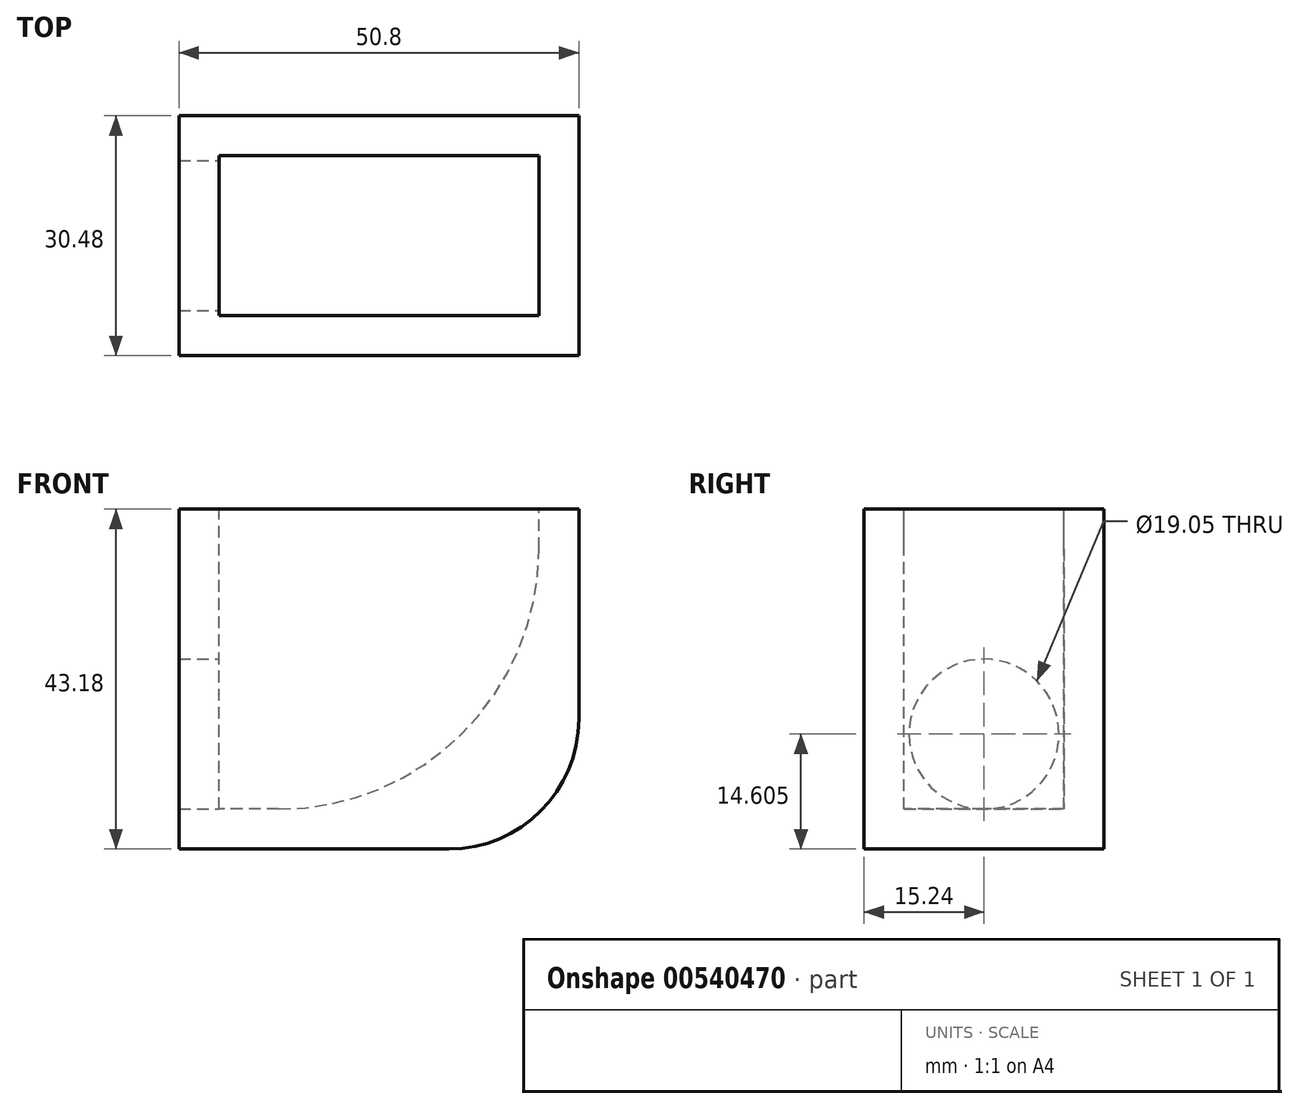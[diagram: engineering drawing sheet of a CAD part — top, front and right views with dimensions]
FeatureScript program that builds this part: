
annotation { "Feature Type Name" : "Feature", "Feature Type Description" : "" }
export const myFeature = defineFeature(function(context is Context, id is Id, definition is map)
    precondition{}
    {
        {
            var Q0;
            Q0=qCreatedBy(makeId("Front.planeOp"),FACE);
            var sketch = newSketch(context, id + "F0", { "sketchPlane" : qUnion([Q0])});
            skLineSegment(sketch, "E0", {"start": v(0, 0) * mm, "end": v(50.8, 0) * mm});
            skLineSegment(sketch, "E1", {"start": v(50.8, 0) * mm, "end": v(50.8, -43.18) * mm});
            skLineSegment(sketch, "E2", {"start": v(50.8, -43.18) * mm, "end": v(0, -43.18) * mm});
            skLineSegment(sketch, "E3", {"start": v(0, 0) * mm, "end": v(0, -43.18) * mm});
            skSolve(sketch);
        }
        {
            var Q0;
            Q0 = qSketchRegion(id + "F0", true);
            extrude(context, id + "F1", {"entities" : qUnion([Q0]), "depth" : 30.48 * mm, "offsetDistance" : 25.4 * mm});
        }
        {
            var Q0;
            Q0=makeQuery(id+"F1.opExtrude","SWEPT_EDGE",EDGE,{"disambiguationData":[OSD([sQuery(id+"F0.wireOp",EDGE,"E1"),sQuery(id+"F0.wireOp",EDGE,"E2")])]});
            fillet(context, id + "F2", {"entities" : qUnion([Q0]), "radius" : 16.5 * mm, "tangentPropagation" : true, "allowEdgeOverflow" : false});
        }
        {
            var Q0;
            Q0=makeQuery(id+"F1.opExtrude","SWEPT_FACE",FACE,{"disambiguationData":[OSD([sQuery(id+"F0.wireOp",EDGE,"E0")])]});
            var sketch = newSketch(context, id + "F3", { "sketchPlane" : qUnion([Q0])});
            skLineSegment(sketch, "E4", {"start": v(5.08, -5.08) * mm, "end": v(5.08, -25.4) * mm});
            skLineSegment(sketch, "E5", {"start": v(5.08, -25.4) * mm, "end": v(45.72, -25.4) * mm});
            skLineSegment(sketch, "E6", {"start": v(45.72, -25.4) * mm, "end": v(45.72, -5.08) * mm});
            skLineSegment(sketch, "E7", {"start": v(45.72, -5.08) * mm, "end": v(5.08, -5.08) * mm});
            skSolve(sketch);
        }
        {
            var Q0;
            Q0=makeQuery(id+"F3.imprint","IMPRINT",FACE,{"disambiguationData":[TD([[makeQuery(id+"F3.imprint","IMPRINT",EDGE,{"derivedFrom":sQuery(id+"F3.wireOp",EDGE,"E4")}),1.0]])]});
            extrude(context, id + "F4", {"entities" : qUnion([Q0]), "operationType" : NewBodyOperationType.REMOVE, "oppositeDirection" : true, "depth" : 38.1 * mm, "offsetDistance" : 25.4 * mm});
        }
        {
            var Q0;
            Q0=makeQuery(id+"F1.opExtrude","SWEPT_FACE",FACE,{"disambiguationData":[OSD([sQuery(id+"F0.wireOp",EDGE,"E3")])]});
            var sketch = newSketch(context, id + "F5", { "sketchPlane" : qUnion([Q0])});
            skCircle(sketch, "E8", {"center": v(15.24, -33.66) * mm, "radius": 9.53 * mm});
            skPoint(sketch, "E8.centerSnap0", {"position": v(15.24, -43.18) * mm});
            skSolve(sketch);
        }
        {
            var Q0;
            Q0=makeQuery(id+"F5.imprint","IMPRINT",FACE,{"disambiguationData":[TD([[makeQuery(id+"F5.imprint","IMPRINT",EDGE,{"derivedFrom":sQuery(id+"F5.wireOp",EDGE,"E8")}),1.0]])]});
            extrude(context, id + "F6", {"entities" : qUnion([Q0]), "operationType" : NewBodyOperationType.ADD, "oppositeDirection" : true, "depth" : 2.54 * mm, "offsetDistance" : 25.4 * mm});
        }
        {
            var Q0;
            Q0=makeQuery(id+"F4.boolean.opBoolean","COPY",EDGE,{"derivedFrom":makeQuery(id+"F4.opExtrude","CAP_EDGE",EDGE,{"disambiguationData":[OSD([sQuery(id+"F3.wireOp",EDGE,"E6")])],"isStart":false})});
            fillet(context, id + "F7", {"entities" : qUnion([Q0]), "radius" : 33.02 * mm, "tangentPropagation" : true, "allowEdgeOverflow" : false});
        }
        {
            var Q0;
            Q0=makeQuery(id+"F4.boolean.opBoolean","COPY",FACE,{"derivedFrom":makeQuery(id+"F4.opExtrude","SWEPT_FACE",FACE,{"disambiguationData":[OSD([sQuery(id+"F3.wireOp",EDGE,"E4")])]})});
            var sketch = newSketch(context, id + "F8", { "sketchPlane" : qUnion([Q0])});
            skCircle(sketch, "E9", {"center": v(-15.24, -28.58) * mm, "radius": 9.53 * mm});
            skPoint(sketch, "E9.centerSnap0", {"position": v(-15.24, -38.1) * mm});
            skSolve(sketch);
        }
        {
            var Q0;
            Q0 = qSketchRegion(id + "F8", true);
            extrude(context, id + "F9", {"entities" : qUnion([Q0]), "operationType" : NewBodyOperationType.REMOVE, "oppositeDirection" : true, "depth" : 25.4 * mm, "offsetDistance" : 25.4 * mm});
        }
    });
